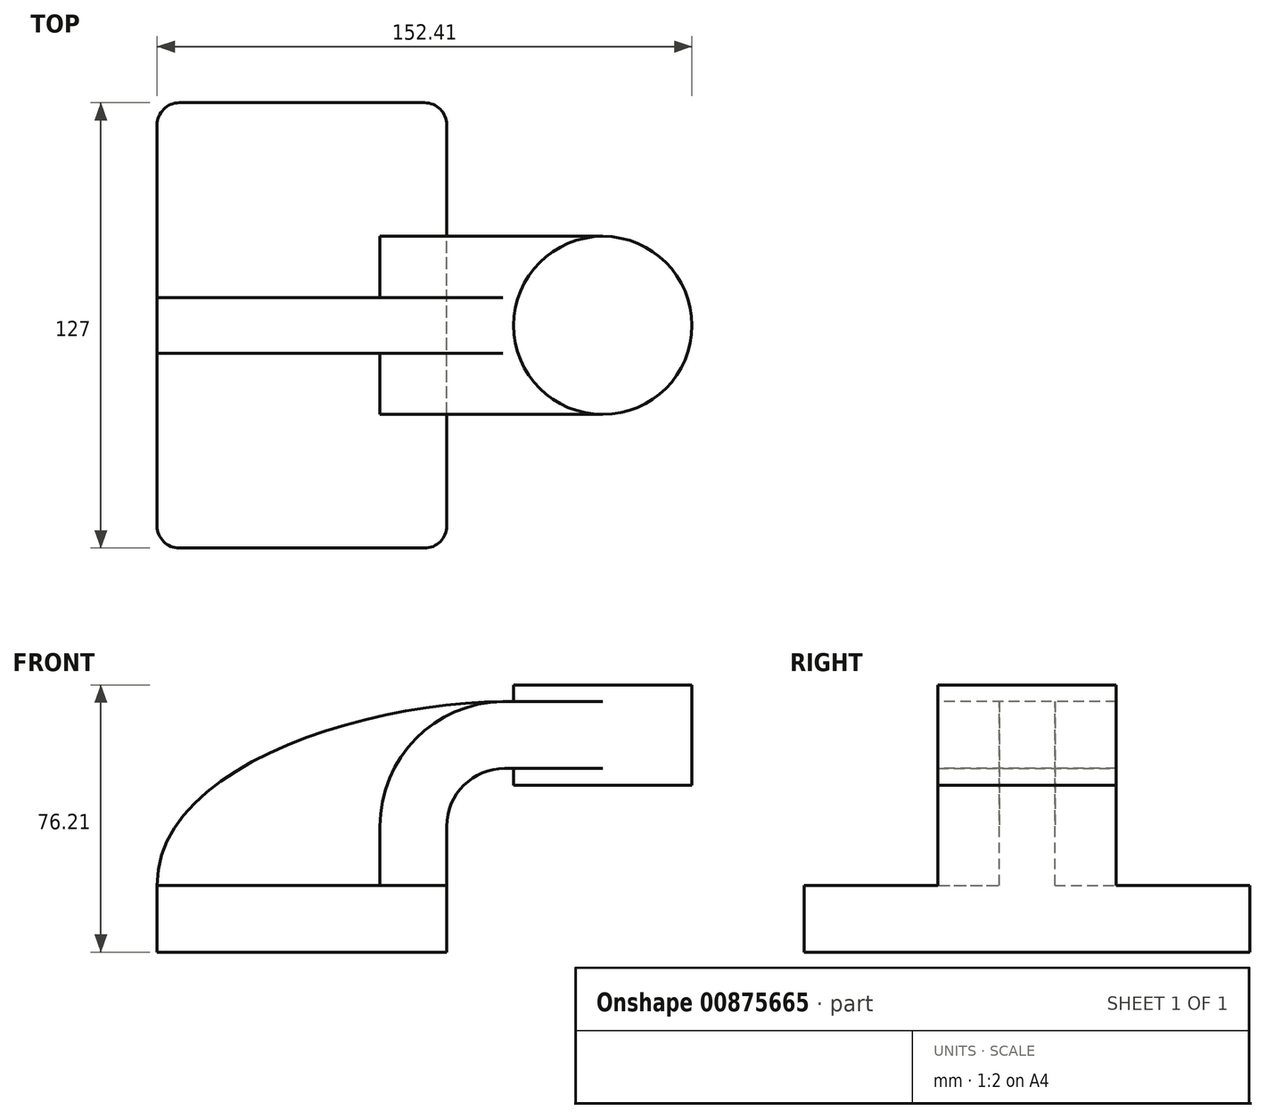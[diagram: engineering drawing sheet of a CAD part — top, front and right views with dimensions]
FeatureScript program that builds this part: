
annotation { "Feature Type Name" : "Feature", "Feature Type Description" : "" }
export const myFeature = defineFeature(function(context is Context, id is Id, definition is map)
    precondition{}
    {
        {
            var Q0;
            Q0=qCreatedBy(makeId("Front.planeOp"),FACE);
            var sketch = newSketch(context, id + "F0", { "sketchPlane" : qUnion([Q0])});
            skLineSegment(sketch, "E0.bottom", {"start": v(41.27, 9.53) * mm, "end": v(-41.28, 9.53) * mm});
            skLineSegment(sketch, "E0.top", {"start": v(41.28, -9.52) * mm, "end": v(-41.27, -9.52) * mm});
            skLineSegment(sketch, "E0.left", {"start": v(41.28, 9.53) * mm, "end": v(41.28, -9.52) * mm});
            skLineSegment(sketch, "E0.right", {"start": v(-41.28, 9.53) * mm, "end": v(-41.28, -9.52) * mm});
            skPoint(sketch, "E0.middle", {"position": v(0, 0) * mm});
            skLineSegment(sketch, "E1.bottom", {"start": v(60.32, 66.68) * mm, "end": v(111.12, 66.68) * mm});
            skLineSegment(sketch, "E1.top", {"start": v(60.33, 38.1) * mm, "end": v(111.12, 38.1) * mm});
            skLineSegment(sketch, "E1.left", {"start": v(60.32, 66.68) * mm, "end": v(60.33, 38.1) * mm});
            skLineSegment(sketch, "E1.right", {"start": v(111.12, 66.68) * mm, "end": v(111.12, 38.1) * mm});
            skPoint(sketch, "E1.middle", {"position": v(85.72, 52.39) * mm});
            skLineSegment(sketch, "E2", {"start": v(41.27, 9.53) * mm, "end": v(41.27, 26.37) * mm});
            skArc(sketch, "E3", {"start": v(41.27, 26.37) * mm, "mid": v(46.11, 38.04) * mm, "end": v(57.78, 42.88) * mm});
            skLineSegment(sketch, "E4", {"start": v(57.78, 42.88) * mm, "end": v(85.72, 42.88) * mm});
            skLineSegment(sketch, "E5.0", {"start": v(57.78, 61.93) * mm, "end": v(85.72, 61.93) * mm});
            skArc(sketch, "E5.1", {"start": v(22.22, 26.37) * mm, "mid": v(32.64, 51.5) * mm, "end": v(57.78, 61.93) * mm});
            skLineSegment(sketch, "E5.2", {"start": v(22.22, 9.53) * mm, "end": v(22.22, 26.37) * mm});
            skLineSegment(sketch, "E6", {"start": v(85.72, 61.93) * mm, "end": v(85.72, 42.88) * mm});
            skLineSegment(sketch, "E7", {"start": v(85.72, 66.68) * mm, "end": v(85.72, 38.1) * mm});
            skFitSpline(sketch, "E8", {"points": [v(-41.28, 9.53) * mm, v(57.79, 61.93) * mm], "startDerivative": vector(-0.63, 102.76) * mm, "endDerivative": vector(117.7, 0.65) * mm});
            skSolve(sketch);
        }
        {
            var Q0;
            Q0=makeQuery(id+"F0.imprint","IMPRINT",FACE,{"disambiguationData":[TD([[makeQuery(id+"F0.imprint","IMPRINT",EDGE,{"derivedFrom":sQuery(id+"F0.wireOp",EDGE,"E0.top")}),-1.0]])]});
            extrude(context, id + "F1", {"entities" : qUnion([Q0]), "endBound" : BoundingType.SYMMETRIC, "depth" : 127 * mm, "offsetDistance" : 25.4 * mm});
        }
        {
            var Q0;
            {var subQ1=sQuery(id+"F0.wireOp",EDGE,"E2");Q0=makeQuery(id+"F0.imprint","IMPRINT",FACE,{"disambiguationData":[TD([[makeQuery(id+"F0.imprint","IMPRINT",EDGE,{"derivedFrom":subQ1}),1.0]])]});}
            var Q1;
            {var subQ0=sQuery(id+"F0.wireOp",EDGE,"E5.0");var subQ1=sQuery(id+"F0.wireOp",EDGE,"E1.left");var subQ2=makeQuery(id+"F0.imprint","INTERSECT",VERTEX,{"derivedFrom":[subQ1,subQ0]});Q1=makeQuery(id+"F0.imprint","IMPRINT",FACE,{"disambiguationData":[TD([[makeQuery(id+"F0.imprint","IMPRINT",EDGE,{"disambiguationData":[TD([[subQ2,-1.0]])],"derivedFrom":subQ1}),1.0]])]});}
            extrude(context, id + "F2", {"entities" : qUnion([Q0, Q1]), "operationType" : NewBodyOperationType.ADD, "endBound" : BoundingType.SYMMETRIC, "depth" : 50.8 * mm, "offsetDistance" : 25.4 * mm});
        }
        {
            var Q0;
            {var subQ3=sQuery(id+"F0.wireOp",EDGE,"E5.2");Q0=makeQuery(id+"F0.imprint","IMPRINT",FACE,{"disambiguationData":[TD([[makeQuery(id+"F0.imprint","IMPRINT",EDGE,{"derivedFrom":subQ3}),1.0]])]});}
            extrude(context, id + "F3", {"entities" : qUnion([Q0]), "operationType" : NewBodyOperationType.ADD, "endBound" : BoundingType.SYMMETRIC, "depth" : 15.88 * mm, "offsetDistance" : 25.4 * mm});
        }
        {
            var Q0;
            {var subQ4=sQuery(id+"F0.wireOp",EDGE,"E1.right");Q0=makeQuery(id+"F0.imprint","IMPRINT",FACE,{"disambiguationData":[TD([[makeQuery(id+"F0.imprint","IMPRINT",EDGE,{"derivedFrom":subQ4}),-1.0]])]});}
            var Q1;
            Q1=sQuery(id+"F0.wireOp",EDGE,"E7");
            revolve(context, id + "F4", {"operationType" : NewBodyOperationType.ADD, "surfaceOperationType" : NewSurfaceOperationType.NEW, "entities" : qUnion([Q0]), "axis" : qUnion([Q1]), "revolveType" : RevolveType.FULL});
        }
        {
            var Q0;
            Q0=makeQuery(id+"F1.opExtrude","CAP_EDGE",EDGE,{"disambiguationData":[OSD([sQuery(id+"F0.wireOp",EDGE,"E0.left")])],"isStart":false});
            var Q1;
            Q1=makeQuery(id+"F1.opExtrude","CAP_EDGE",EDGE,{"disambiguationData":[OSD([sQuery(id+"F0.wireOp",EDGE,"E0.right")])],"isStart":false});
            var Q2;
            Q2=makeQuery(id+"F1.opExtrude","CAP_EDGE",EDGE,{"disambiguationData":[OSD([sQuery(id+"F0.wireOp",EDGE,"E0.left")])],"isStart":true});
            var Q3;
            Q3=makeQuery(id+"F1.opExtrude","CAP_EDGE",EDGE,{"disambiguationData":[OSD([sQuery(id+"F0.wireOp",EDGE,"E0.right")])],"isStart":true});
            fillet(context, id + "F5", {"entities" : qUnion([Q0, Q1, Q2, Q3]), "radius" : 6.35 * mm, "tangentPropagation" : true, "allowEdgeOverflow" : false});
        }
    });
